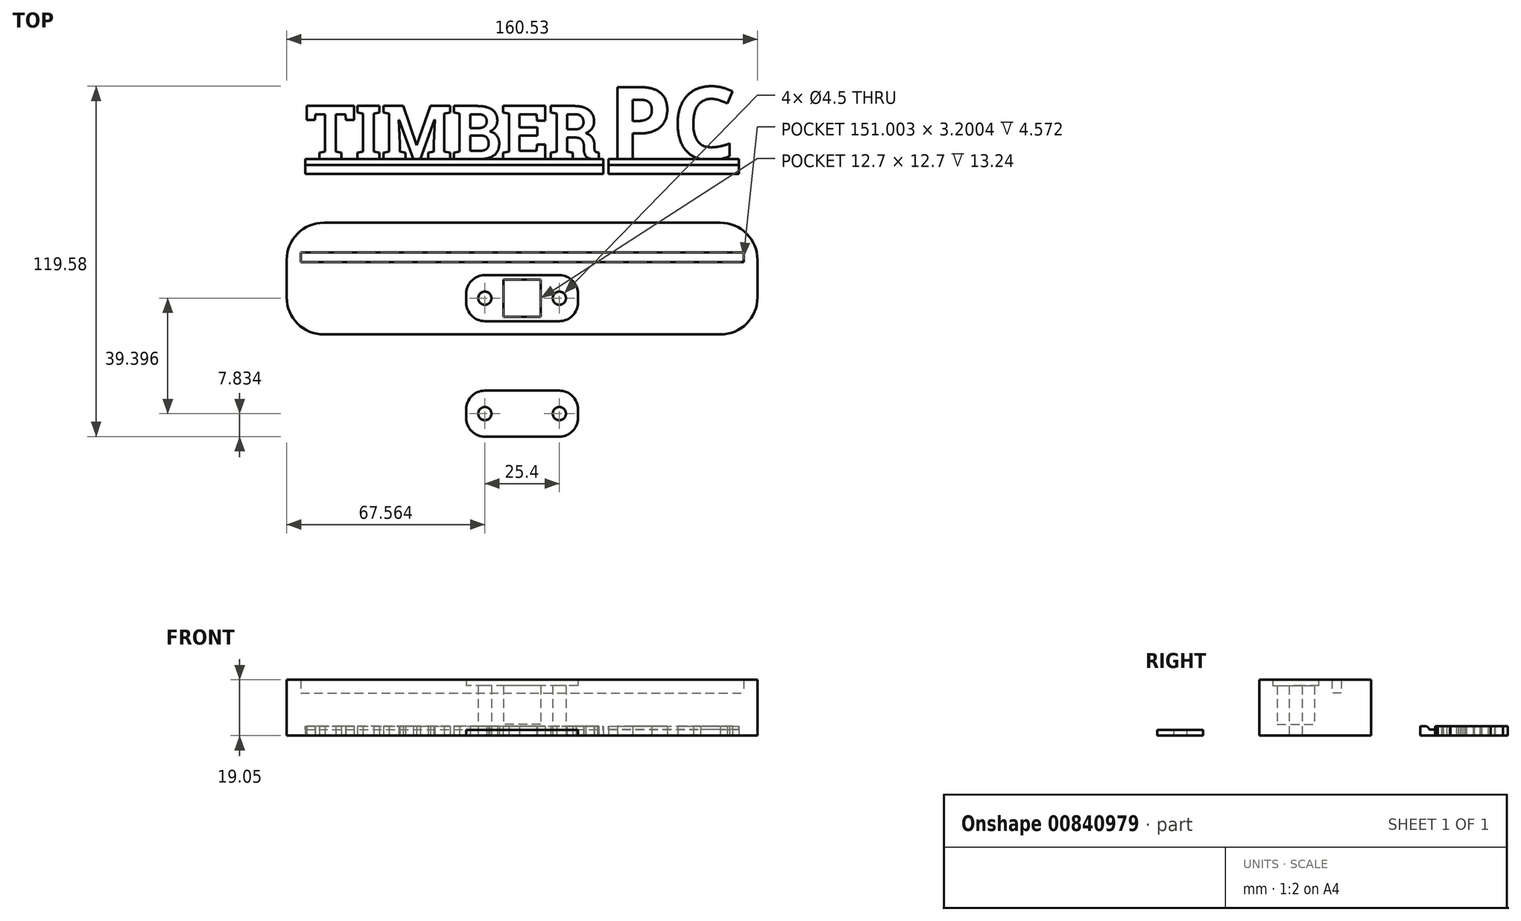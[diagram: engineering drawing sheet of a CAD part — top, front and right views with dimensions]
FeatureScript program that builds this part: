
annotation { "Feature Type Name" : "Feature", "Feature Type Description" : "" }
export const myFeature = defineFeature(function(context is Context, id is Id, definition is map)
    precondition{}
    {
        {
            var Q0;
            Q0=qCreatedBy(makeId("Top.planeOp"),FACE);
            var sketch = newSketch(context, id + "F0", { "sketchPlane" : qUnion([Q0])});
            skText(sketch, "E0", { "text": "TIMBER", "fontName": "RobotoSlab-Bold.ttf"});
            skText(sketch, "E1", { "text": "PC", "fontName": "OpenSans-Bold.ttf"});
            skLineSegment(sketch, "E2.bottom", {"start": v(-74.93, 22.1) * mm, "end": v(26.67, 22.1) * mm});
            skLineSegment(sketch, "E2.top", {"start": v(-74.93, 17.02) * mm, "end": v(26.67, 17.02) * mm});
            skLineSegment(sketch, "E2.left", {"start": v(-74.93, 22.1) * mm, "end": v(-74.93, 17.02) * mm});
            skLineSegment(sketch, "E2.right", {"start": v(26.67, 22.1) * mm, "end": v(26.67, 17.02) * mm});
            skLineSegment(sketch, "E3.bottom", {"start": v(28.45, 22.1) * mm, "end": v(72.9, 22.1) * mm});
            skLineSegment(sketch, "E3.top", {"start": v(28.45, 17.02) * mm, "end": v(72.9, 17.02) * mm});
            skLineSegment(sketch, "E3.left", {"start": v(28.45, 22.1) * mm, "end": v(28.45, 17.02) * mm});
            skLineSegment(sketch, "E3.right", {"start": v(72.9, 22.1) * mm, "end": v(72.9, 17.02) * mm});
            skLineSegment(sketch, "E4.top", {"start": v(-74.93, 20.1) * mm, "end": v(26.67, 20.1) * mm});
            skLineSegment(sketch, "E4.left", {"start": v(-74.93, 22.1) * mm, "end": v(-74.93, 20.1) * mm});
            skLineSegment(sketch, "E4.right", {"start": v(26.67, 22.1) * mm, "end": v(26.67, 20.1) * mm});
            skLineSegment(sketch, "E5.top", {"start": v(28.45, 20.1) * mm, "end": v(72.9, 20.1) * mm});
            skLineSegment(sketch, "E5.left", {"start": v(28.45, 22.1) * mm, "end": v(28.45, 20.1) * mm});
            skLineSegment(sketch, "E5.right", {"start": v(72.9, 22.1) * mm, "end": v(72.9, 20.1) * mm});
            const initialGuessF0  = {"E0": [-0.07493, 0.0221, 1, 0, 0.01833], "E1": [0.02845, 0.0221, 1, 0, 0.02472]};
            skSetInitialGuess(sketch, initialGuessF0);
            skSolve(sketch);
        }
        {
            var Q0;
            Q0=makeQuery(id+"F0.imprint","IMPRINT",FACE,{"disambiguationData":[TD([[makeQuery(id+"F0.imprint","IMPRINT",EDGE,{"derivedFrom":sQuery(id+"F0.wireOp",EDGE,"E0.sketch_text.stroke-0")}),-1.0]])]});
            var Q1;
            Q1=makeQuery(id+"F0.imprint","IMPRINT",FACE,{"disambiguationData":[TD([[makeQuery(id+"F0.imprint","IMPRINT",EDGE,{"derivedFrom":sQuery(id+"F0.wireOp",EDGE,"E0.sketch_text.stroke-16")}),-1.0]])]});
            var Q2;
            Q2=makeQuery(id+"F0.imprint","IMPRINT",FACE,{"disambiguationData":[TD([[makeQuery(id+"F0.imprint","IMPRINT",EDGE,{"derivedFrom":sQuery(id+"F0.wireOp",EDGE,"E0.sketch_text.stroke-89")}),-1.0]])]});
            var Q3;
            Q3=makeQuery(id+"F0.imprint","IMPRINT",FACE,{"disambiguationData":[TD([[makeQuery(id+"F0.imprint","IMPRINT",EDGE,{"derivedFrom":sQuery(id+"F0.wireOp",EDGE,"E1.sketch_text.stroke-16")}),-1.0]])]});
            var Q4;
            Q4=makeQuery(id+"F0.imprint","IMPRINT",FACE,{"disambiguationData":[TD([[makeQuery(id+"F0.imprint","IMPRINT",EDGE,{"derivedFrom":sQuery(id+"F0.wireOp",EDGE,"E2.top")}),1.0]])]});
            var Q5;
            Q5=makeQuery(id+"F0.imprint","IMPRINT",FACE,{"disambiguationData":[TD([[makeQuery(id+"F0.imprint","IMPRINT",EDGE,{"derivedFrom":sQuery(id+"F0.wireOp",EDGE,"E3.top")}),1.0]])]});
            var Q6;
            Q6=makeQuery(id+"F0.imprint","IMPRINT",FACE,{"disambiguationData":[TD([[makeQuery(id+"F0.imprint","IMPRINT",EDGE,{"derivedFrom":sQuery(id+"F0.wireOp",EDGE,"E1.sketch_text.stroke-0")}),-1.0]])]});
            var Q7;
            {var subQ0=sQuery(id+"F0.wireOp",EDGE,"E1.sketch_text.stroke-22");var subQ1=sQuery(id+"F0.wireOp",EDGE,"E1.sketch_text.stroke-21");var subQ2=makeQuery(id+"F0.imprint","INTERSECT",VERTEX,{"derivedFrom":[subQ1,subQ0]});Q7=makeQuery(id+"F0.imprint","IMPRINT",FACE,{"disambiguationData":[TD([[makeQuery(id+"F0.imprint","IMPRINT",EDGE,{"disambiguationData":[TD([[subQ2,1.0]])],"derivedFrom":subQ1}),-1.0]])]});}
            var Q8;
            Q8=makeQuery(id+"F0.imprint","IMPRINT",FACE,{"disambiguationData":[TD([[makeQuery(id+"F0.imprint","IMPRINT",EDGE,{"derivedFrom":sQuery(id+"F0.wireOp",EDGE,"E0.sketch_text.stroke-28")}),-1.0]])]});
            var Q9;
            Q9=makeQuery(id+"F0.imprint","IMPRINT",FACE,{"disambiguationData":[TD([[makeQuery(id+"F0.imprint","IMPRINT",EDGE,{"derivedFrom":sQuery(id+"F0.wireOp",EDGE,"E0.sketch_text.stroke-59")}),-1.0]])]});
            var Q10;
            Q10=makeQuery(id+"F0.imprint","IMPRINT",FACE,{"disambiguationData":[TD([[makeQuery(id+"F0.imprint","IMPRINT",EDGE,{"derivedFrom":sQuery(id+"F0.wireOp",EDGE,"E0.sketch_text.stroke-110")}),-1.0]])]});
            var Q11;
            Q11=makeQuery(id+"F0.imprint","IMPRINT",FACE,{"disambiguationData":[TD([[makeQuery(id+"F0.imprint","IMPRINT",EDGE,{"derivedFrom":sQuery(id+"F0.wireOp",EDGE,"E5.top")}),1.0]])]});
            var Q12;
            Q12=makeQuery(id+"F0.imprint","IMPRINT",FACE,{"disambiguationData":[TD([[makeQuery(id+"F0.imprint","IMPRINT",EDGE,{"derivedFrom":sQuery(id+"F0.wireOp",EDGE,"E4.top")}),1.0]])]});
            extrude(context, id + "F1", {"entities" : qUnion([Q0, Q1, Q2, Q3, Q4, Q5, Q6, Q7, Q8, Q9, Q10, Q11, Q12]), "depth" : 2.12 * mm, "offsetDistance" : 25.4 * mm});
        }
        {
            var Q0;
            Q0=makeQuery(id+"F0.imprint","IMPRINT",FACE,{"disambiguationData":[TD([[makeQuery(id+"F0.imprint","IMPRINT",EDGE,{"derivedFrom":sQuery(id+"F0.wireOp",EDGE,"E0.sketch_text.stroke-0")}),-1.0]])]});
            var Q1;
            Q1=makeQuery(id+"F0.imprint","IMPRINT",FACE,{"disambiguationData":[TD([[makeQuery(id+"F0.imprint","IMPRINT",EDGE,{"derivedFrom":sQuery(id+"F0.wireOp",EDGE,"E0.sketch_text.stroke-16")}),-1.0]])]});
            var Q2;
            Q2=makeQuery(id+"F0.imprint","IMPRINT",FACE,{"disambiguationData":[TD([[makeQuery(id+"F0.imprint","IMPRINT",EDGE,{"derivedFrom":sQuery(id+"F0.wireOp",EDGE,"E0.sketch_text.stroke-28")}),-1.0]])]});
            var Q3;
            Q3=makeQuery(id+"F0.imprint","IMPRINT",FACE,{"disambiguationData":[TD([[makeQuery(id+"F0.imprint","IMPRINT",EDGE,{"derivedFrom":sQuery(id+"F0.wireOp",EDGE,"E0.sketch_text.stroke-59")}),-1.0]])]});
            var Q4;
            Q4=makeQuery(id+"F0.imprint","IMPRINT",FACE,{"disambiguationData":[TD([[makeQuery(id+"F0.imprint","IMPRINT",EDGE,{"derivedFrom":sQuery(id+"F0.wireOp",EDGE,"E0.sketch_text.stroke-89")}),-1.0]])]});
            var Q5;
            Q5=makeQuery(id+"F0.imprint","IMPRINT",FACE,{"disambiguationData":[TD([[makeQuery(id+"F0.imprint","IMPRINT",EDGE,{"derivedFrom":sQuery(id+"F0.wireOp",EDGE,"E0.sketch_text.stroke-110")}),-1.0]])]});
            var Q6;
            Q6=makeQuery(id+"F0.imprint","IMPRINT",FACE,{"disambiguationData":[TD([[makeQuery(id+"F0.imprint","IMPRINT",EDGE,{"derivedFrom":sQuery(id+"F0.wireOp",EDGE,"E2.top")}),1.0]])]});
            extrude(context, id + "F2", {"entities" : qUnion([Q0, Q1, Q2, Q3, Q4, Q5, Q6]), "operationType" : NewBodyOperationType.ADD, "depth" : 3.17 * mm, "offsetDistance" : 25.4 * mm});
        }
        {
            var Q0;
            Q0=makeQuery(id+"F0.imprint","IMPRINT",FACE,{"disambiguationData":[TD([[makeQuery(id+"F0.imprint","IMPRINT",EDGE,{"derivedFrom":sQuery(id+"F0.wireOp",EDGE,"E1.sketch_text.stroke-0")}),-1.0]])]});
            var Q1;
            Q1=makeQuery(id+"F0.imprint","IMPRINT",FACE,{"disambiguationData":[TD([[makeQuery(id+"F0.imprint","IMPRINT",EDGE,{"derivedFrom":sQuery(id+"F0.wireOp",EDGE,"E1.sketch_text.stroke-16")}),-1.0]])]});
            var Q2;
            Q2=makeQuery(id+"F0.imprint","IMPRINT",FACE,{"disambiguationData":[TD([[makeQuery(id+"F0.imprint","IMPRINT",EDGE,{"derivedFrom":sQuery(id+"F0.wireOp",EDGE,"E3.top")}),1.0]])]});
            extrude(context, id + "F3", {"entities" : qUnion([Q0, Q1, Q2]), "operationType" : NewBodyOperationType.ADD, "depth" : 3.17 * mm, "offsetDistance" : 25.4 * mm});
        }
        {
            var Q0;
            Q0=makeQuery(id+"F2.opExtrude","CAP_EDGE",EDGE,{"disambiguationData":[OSD([sQuery(id+"F0.wireOp",EDGE,"E4.top")])],"isStart":false});
            var Q1;
            Q1=makeQuery(id+"F3.opExtrude","CAP_EDGE",EDGE,{"disambiguationData":[OSD([sQuery(id+"F0.wireOp",EDGE,"E5.top")])],"isStart":false});
            fillet(context, id + "F4", {"entities" : qUnion([Q0, Q1]), "radius" : 1.27 * mm, "tangentPropagation" : true, "allowEdgeOverflow" : false});
        }
        {
            var Q0;
            Q0=qCreatedBy(makeId("Top.planeOp"),FACE);
            var sketch = newSketch(context, id + "F5", { "sketchPlane" : qUnion([Q0])});
            skPoint(sketch, "E6.0", {"position": v(-74.93, 17.02) * mm});
            skPoint(sketch, "E6.1", {"position": v(72.9, 17.02) * mm});
            skLineSegment(sketch, "E7.bottom", {"start": v(-68.58, 0.33) * mm, "end": v(66.55, 0.33) * mm});
            skLineSegment(sketch, "E7.top", {"start": v(-68.58, -37.77) * mm, "end": v(66.55, -37.77) * mm});
            skLineSegment(sketch, "E7.left", {"start": v(-81.28, -12.37) * mm, "end": v(-81.28, -25.07) * mm});
            skLineSegment(sketch, "E7.right", {"start": v(79.25, -12.37) * mm, "end": v(79.25, -25.07) * mm});
            skLineSegment(sketch, "E8.bottom", {"start": v(-76.52, -9.83) * mm, "end": v(74.49, -9.83) * mm});
            skLineSegment(sketch, "E8.top", {"start": v(-76.52, -13.03) * mm, "end": v(74.49, -13.03) * mm});
            skLineSegment(sketch, "E8.left", {"start": v(-76.52, -9.83) * mm, "end": v(-76.52, -13.03) * mm});
            skLineSegment(sketch, "E8.right", {"start": v(74.49, -9.83) * mm, "end": v(74.49, -13.03) * mm});
            skPoint(sketch, "E9.visualSharp", {"position": v(-81.28, 0.33) * mm});
            skArc(sketch, "E9.filletArc", {"start": v(-68.58, 0.33) * mm, "mid": v(-77.56, -3.4) * mm, "end": v(-81.28, -12.37) * mm});
            skPoint(sketch, "E10.visualSharp", {"position": v(-81.28, -37.77) * mm});
            skArc(sketch, "E10.filletArc", {"start": v(-81.28, -25.07) * mm, "mid": v(-77.56, -34.05) * mm, "end": v(-68.58, -37.77) * mm});
            skPoint(sketch, "E11.visualSharp", {"position": v(79.25, 0.33) * mm});
            skArc(sketch, "E11.filletArc", {"start": v(79.25, -12.37) * mm, "mid": v(75.53, -3.4) * mm, "end": v(66.55, 0.33) * mm});
            skPoint(sketch, "E12.visualSharp", {"position": v(79.25, -37.77) * mm});
            skArc(sketch, "E12.filletArc", {"start": v(66.55, -37.77) * mm, "mid": v(75.53, -34.05) * mm, "end": v(79.25, -25.07) * mm});
            skLineSegment(sketch, "E13.bottom", {"start": v(5.33, -31.74) * mm, "end": v(-7.37, -31.74) * mm});
            skLineSegment(sketch, "E13.top", {"start": v(5.33, -19.04) * mm, "end": v(-7.37, -19.04) * mm});
            skLineSegment(sketch, "E13.left", {"start": v(5.33, -31.74) * mm, "end": v(5.33, -19.04) * mm});
            skLineSegment(sketch, "E13.right", {"start": v(-7.37, -31.74) * mm, "end": v(-7.37, -19.04) * mm});
            skPoint(sketch, "E13.middle", {"position": v(-1.02, -25.4) * mm});
            skPoint(sketch, "E13.middle.positionSnap0", {"position": v(-1.02, -37.77) * mm});
            skPoint(sketch, "E13.centerSnap0", {"position": v(-1.02, -37.77) * mm});
            skLineSegment(sketch, "E14.bottom", {"start": v(11.68, -33.23) * mm, "end": v(-13.72, -33.23) * mm});
            skLineSegment(sketch, "E14.top", {"start": v(11.68, -17.55) * mm, "end": v(-13.72, -17.55) * mm});
            skLineSegment(sketch, "E14.left", {"start": v(18.03, -26.88) * mm, "end": v(18.03, -23.9) * mm});
            skLineSegment(sketch, "E14.right", {"start": v(-20.07, -26.88) * mm, "end": v(-20.07, -23.9) * mm});
            skCircle(sketch, "E15", {"center": v(-13.72, -25.4) * mm, "radius": 2.25 * mm});
            skCircle(sketch, "E16", {"center": v(11.68, -25.4) * mm, "radius": 2.25 * mm});
            skPoint(sketch, "E17.visualSharp", {"position": v(-20.07, -17.55) * mm});
            skArc(sketch, "E17.filletArc", {"start": v(-13.72, -17.55) * mm, "mid": v(-18.2, -19.41) * mm, "end": v(-20.07, -23.9) * mm});
            skPoint(sketch, "E18.visualSharp", {"position": v(-20.07, -33.23) * mm});
            skArc(sketch, "E18.filletArc", {"start": v(-20.07, -26.88) * mm, "mid": v(-18.2, -31.37) * mm, "end": v(-13.72, -33.23) * mm});
            skPoint(sketch, "E19.visualSharp", {"position": v(18.03, -17.55) * mm});
            skArc(sketch, "E19.filletArc", {"start": v(18.03, -23.9) * mm, "mid": v(16.17, -19.41) * mm, "end": v(11.68, -17.55) * mm});
            skPoint(sketch, "E20.visualSharp", {"position": v(18.03, -33.23) * mm});
            skArc(sketch, "E20.filletArc", {"start": v(11.68, -33.23) * mm, "mid": v(16.17, -31.37) * mm, "end": v(18.03, -26.88) * mm});
            skSolve(sketch);
        }
        {
            var Q0;
            Q0=makeQuery(id+"F5.imprint","IMPRINT",FACE,{"disambiguationData":[TD([[makeQuery(id+"F5.imprint","IMPRINT",EDGE,{"derivedFrom":sQuery(id+"F5.wireOp",EDGE,"E7.bottom")}),-1.0]])]});
            extrude(context, id + "F6", {"entities" : qUnion([Q0]), "depth" : 19.05 * mm, "offsetDistance" : 25.4 * mm});
        }
        {
            var Q0;
            Q0=makeQuery(id+"F5.imprint","IMPRINT",FACE,{"disambiguationData":[TD([[makeQuery(id+"F5.imprint","IMPRINT",EDGE,{"derivedFrom":sQuery(id+"F5.wireOp",EDGE,"E8.bottom")}),-1.0]])]});
            extrude(context, id + "F7", {"entities" : qUnion([Q0]), "operationType" : NewBodyOperationType.ADD, "depth" : 14.48 * mm, "offsetDistance" : 25.4 * mm});
        }
        {
            var Q0;
            Q0=makeQuery(id+"F5.imprint","IMPRINT",FACE,{"disambiguationData":[TD([[makeQuery(id+"F5.imprint","IMPRINT",EDGE,{"derivedFrom":sQuery(id+"F5.wireOp",EDGE,"E13.bottom")}),1.0]])]});
            extrude(context, id + "F8", {"entities" : qUnion([Q0]), "operationType" : NewBodyOperationType.ADD, "depth" : 17.05 * mm, "offsetDistance" : 25.4 * mm});
        }
        {
            var Q0;
            Q0=makeQuery(id+"F5.imprint","IMPRINT",FACE,{"disambiguationData":[TD([[makeQuery(id+"F5.imprint","IMPRINT",EDGE,{"derivedFrom":sQuery(id+"F5.wireOp",EDGE,"E13.bottom")}),-1.0]])]});
            extrude(context, id + "F9", {"entities" : qUnion([Q0]), "operationType" : NewBodyOperationType.ADD, "depth" : 3.8 * mm, "offsetDistance" : 25.4 * mm});
        }
        {
            var Q0;
            Q0=qCreatedBy(makeId("Top.planeOp"),FACE);
            var sketch = newSketch(context, id + "F10", { "sketchPlane" : qUnion([Q0])});
            skPoint(sketch, "E21.0", {"position": v(-20.07, -33.23) * mm});
            skPoint(sketch, "E21.1", {"position": v(-13.72, -25.4) * mm});
            skPoint(sketch, "E21.2", {"position": v(11.68, -25.4) * mm});
            skPoint(sketch, "E21.3", {"position": v(18.03, -33.23) * mm});
            skLineSegment(sketch, "E22.bottom", {"start": v(-13.72, -56.95) * mm, "end": v(11.68, -56.95) * mm});
            skLineSegment(sketch, "E22.top", {"start": v(-13.72, -72.62) * mm, "end": v(11.68, -72.62) * mm});
            skLineSegment(sketch, "E22.left", {"start": v(-20.07, -63.3) * mm, "end": v(-20.07, -66.27) * mm});
            skLineSegment(sketch, "E22.right", {"start": v(18.03, -63.3) * mm, "end": v(18.03, -66.27) * mm});
            skCircle(sketch, "E23", {"center": v(-13.72, -64.79) * mm, "radius": 2.25 * mm});
            skPoint(sketch, "E23.centerSnap0", {"position": v(-20.07, -64.79) * mm});
            skCircle(sketch, "E24", {"center": v(11.68, -64.79) * mm, "radius": 2.25 * mm});
            skPoint(sketch, "E24.centerSnap0", {"position": v(18.03, -64.79) * mm});
            skPoint(sketch, "E25.visualSharp", {"position": v(-20.07, -56.95) * mm});
            skArc(sketch, "E25.filletArc", {"start": v(-13.72, -56.95) * mm, "mid": v(-18.2, -58.8) * mm, "end": v(-20.07, -63.3) * mm});
            skPoint(sketch, "E26.visualSharp", {"position": v(-20.07, -72.62) * mm});
            skArc(sketch, "E26.filletArc", {"start": v(-20.07, -66.27) * mm, "mid": v(-18.2, -70.76) * mm, "end": v(-13.72, -72.62) * mm});
            skPoint(sketch, "E27.visualSharp", {"position": v(18.03, -56.95) * mm});
            skArc(sketch, "E27.filletArc", {"start": v(18.03, -63.3) * mm, "mid": v(16.17, -58.8) * mm, "end": v(11.68, -56.95) * mm});
            skPoint(sketch, "E28.visualSharp", {"position": v(18.03, -72.62) * mm});
            skArc(sketch, "E28.filletArc", {"start": v(11.68, -72.62) * mm, "mid": v(16.17, -70.76) * mm, "end": v(18.03, -66.27) * mm});
            skSolve(sketch);
        }
        {
            var Q0;
            Q0=makeQuery(id+"F10.imprint","IMPRINT",FACE,{"disambiguationData":[TD([[makeQuery(id+"F10.imprint","IMPRINT",EDGE,{"derivedFrom":sQuery(id+"F10.wireOp",EDGE,"E22.bottom")}),-1.0]])]});
            extrude(context, id + "F11", {"entities" : qUnion([Q0]), "depth" : 2 * mm, "offsetDistance" : 25.4 * mm});
        }
    });
